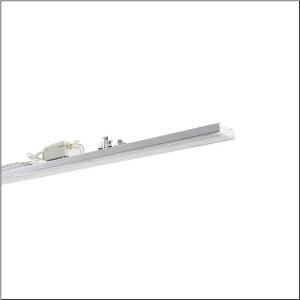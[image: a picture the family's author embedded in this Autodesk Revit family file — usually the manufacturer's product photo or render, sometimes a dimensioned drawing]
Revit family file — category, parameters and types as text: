
# Revit family: licross_r__21_recessed_mo_52te12dn4axg3s_3072
name_source: partatom
category: Lighting Fixtures
units: mm (PartAtom-declared; Revit-internal decimal feet)

## family parameters
Cut with Voids When Loaded = No
Host = Face
Light Source = No
Part Type = Normal
Room Calculation Point = No
Round Connector Dimension = Use Diameter
Shared = No

## types (1)
- --- (1 x LED, 950 lm, 6.7 W, 4000K)
    Apparent Load = 7 VA
    CIE Flux Codes = 72 92 99 100 100
    Color Rendering = 80
    Color Temperature = 4000K
    Default Elevation = 1800 mm
    Description = Licross® 21 Recessed MO, luminaire insert, of sheet steel, galvanised, coil coated, white, length: 1.500mm, width: 66mm, height: 67mm, LED rated luminous flux: 10.280lm, light colour: 840, control gear: DALI 2, with plug, 6-pole, with phase selection, for trunking rail, 14-core, mains connection: 220..240V, AC, 50/60Hz, rated input power: 62W, halogen-free wiring, for emergency light function, for trunking rail, 14-core, converter,control gear: single battery element, battery: LiFeP04, 9Ah, primary optical cover: cover, of PMMA, light emission: direct distribution, primary light characteristic: symmetric, protection rating (complete): IP54, insulation class (complete): insulation class I (protective earthing), certification: CE, UKCA, protection symbol: D if used in an environment with non-conductive dust loads with corresponding accessories, impact resistance: IK06, permissible ambient temperature for indoor applications: +5..+35°C, standard: EN 60598-2-22, LABS conformity tested according to VDMA 24364:2018-05, reducing of maximum allowable ambient temperature of 5°C with ceiling mounting, corresponds to IFS (International Featured Standards) requirements for safety and quality in the food industry, packaging unit: 1 piece
    Height = 58 mm
    Lamp = 1 x LED
    Lamp Light Flux = 950 lm
    Lamp Power = 6.7 W
    Lamp count = 1
    Length = 1500 mm
    Luminous efficacy = 142 lm/W
    Manufacturer = Siteco
    ModVariant = No
    Model = 52TE12DN4AXG3S
    Mounting Place = Ceiling
    Mounting Type = Pendant
    Number of Poles = 1
    OnlyDefault = Yes
    Power Factor = 1
    Product Name = Licross® 21 Recessed MO
    Product group = luminaire insert
    ProductGroupID = 901
    Protection Class = Protection class I
    Protection Degree = IP 54
    RLX_Detail_Level = 1
    RLX_Emergency_Light_Flux = 0 lm
    RLX_Emergency_Type = 0
    RLX_Emergency_Type_DB = No
    RlxData = <blob elided: 24997 chars, md5=578f9135>
    Socket = socket
    Standby Power = 0 W
    System Light Flux = 950 lm
    System Power = 7 W
    Type Comments = : emergency light operation: 3 h
    Type Image = l_1296930.jpg
    URL = http://relux.com
    VarID = @adj_040185
    Voltage = 0 V
    Weight = 0.00 kg
    Width = 66 mm

## geometry (parser evidence)
native form markers: Blend x4, Sweep x11
no freeform markers — native parametric forms only
